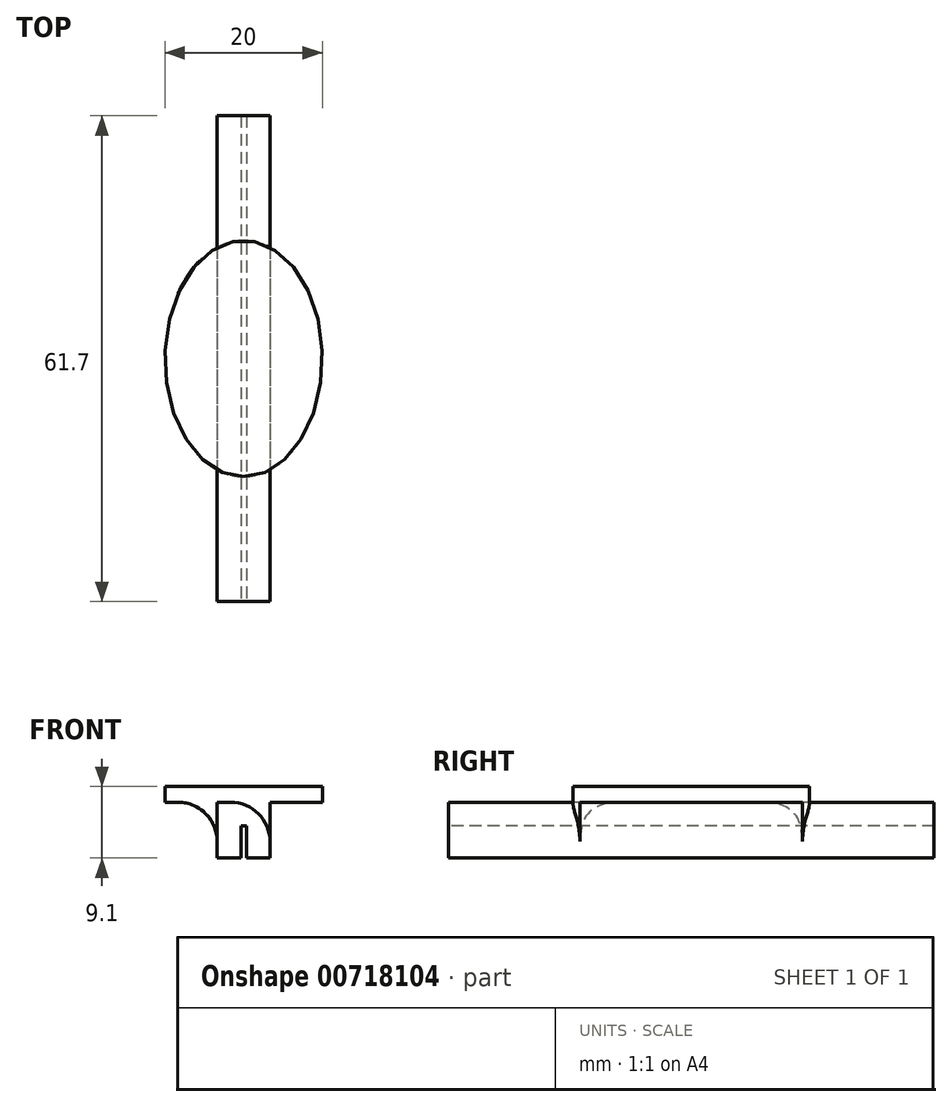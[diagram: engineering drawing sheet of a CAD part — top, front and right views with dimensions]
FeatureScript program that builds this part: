
annotation { "Feature Type Name" : "Feature", "Feature Type Description" : "" }
export const myFeature = defineFeature(function(context is Context, id is Id, definition is map)
    precondition{}
    {
        {
            var Q0;
            Q0=qCreatedBy(makeId("Front.planeOp"),FACE);
            var sketch = newSketch(context, id + "F0", { "sketchPlane" : qUnion([Q0])});
            skLineSegment(sketch, "E0", {"start": v(-3.3, 0) * mm, "end": v(3.93, 0) * mm, "construction": true});
            skLineSegment(sketch, "E1", {"start": v(0, 4.88) * mm, "end": v(0, -4.34) * mm, "construction": true});
            skLineSegment(sketch, "E2", {"start": v(-3.35, 0) * mm, "end": v(-0.35, 0) * mm});
            skLineSegment(sketch, "E3", {"start": v(-0.35, 0) * mm, "end": v(-0.35, 4.1) * mm});
            skLineSegment(sketch, "E4", {"start": v(-0.35, 4.1) * mm, "end": v(0.35, 4.1) * mm});
            skLineSegment(sketch, "E5", {"start": v(0.35, 4.1) * mm, "end": v(0.35, 0) * mm});
            skLineSegment(sketch, "E6", {"start": v(0.35, 0) * mm, "end": v(3.35, 0) * mm});
            skLineSegment(sketch, "E7", {"start": v(3.35, 0) * mm, "end": v(3.35, 7.1) * mm});
            skLineSegment(sketch, "E8", {"start": v(3.35, 7.1) * mm, "end": v(-3.35, 7.1) * mm});
            skLineSegment(sketch, "E9", {"start": v(-3.35, 7.1) * mm, "end": v(-3.35, 0) * mm});
            skSolve(sketch);
        }
        {
            var Q0;
            Q0 = qSketchRegion(id + "F0", true);
            extrude(context, id + "F1", {"entities" : qUnion([Q0]), "oppositeDirection" : true, "depth" : 61.7 * mm, "offsetDistance" : 25 * mm});
        }
        {
            var Q0;
            Q0=makeQuery(id+"F1.opExtrude","SWEPT_FACE",FACE,{"disambiguationData":[OSD([sQuery(id+"F0.wireOp",EDGE,"E8")])]});
            var sketch = newSketch(context, id + "F2", { "sketchPlane" : qUnion([Q0])});
            skEllipse(sketch, "E10", {"center": v(0, 30.85) * mm, "majorRadius": 15 * mm, "minorRadius": 10 * mm, "majorAxis": v(0, -1)});
            skLineSegment(sketch, "E11", {"start": v(0, 56.94) * mm, "end": v(0, -9.97) * mm, "construction": true});
            skPoint(sketch, "E11.endSnap0", {"position": v(0, 15.85) * mm});
            skSolve(sketch);
        }
        {
            var Q0;
            Q0 = qSketchRegion(id + "F2", true);
            extrude(context, id + "F3", {"entities" : qUnion([Q0]), "operationType" : NewBodyOperationType.ADD, "depth" : 2 * mm, "offsetDistance" : 25 * mm});
        }
        {
            var Q0;
            {var subQ0=sQuery(id+"F0.wireOp",EDGE,"E7");Q0=makeQuery(id+"F3.boolean.opBoolean","SPLIT",EDGE,{"disambiguationData":[topologyDisambiguationEdgeConnected([makeQuery(id+"F1.opExtrude","SWEPT_FACE",FACE,{"disambiguationData":[OSD([subQ0])]}),makeQuery(id+"F3.opExtrude","CAP_FACE",FACE,{"disambiguationData":[OSD([sQuery(id+"F2.wireOp",EDGE,"E10")])],"isStart":true})])],"derivedFrom":makeQuery(id+"F1.opExtrude","SWEPT_EDGE",EDGE,{"disambiguationData":[OSD([subQ0,sQuery(id+"F0.wireOp",EDGE,"E8")])]})});}
            fillet(context, id + "F4", {"entities" : qUnion([Q0]), "radius" : 5 * mm, "tangentPropagation" : true, "allowEdgeOverflow" : false});
        }
        {
            var Q0;
            {var subQ0=sQuery(id+"F0.wireOp",EDGE,"E9");Q0=makeQuery(id+"F3.boolean.opBoolean","SPLIT",EDGE,{"disambiguationData":[topologyDisambiguationEdgeConnected([makeQuery(id+"F1.opExtrude","SWEPT_FACE",FACE,{"disambiguationData":[OSD([subQ0])]}),makeQuery(id+"F3.opExtrude","CAP_FACE",FACE,{"disambiguationData":[OSD([sQuery(id+"F2.wireOp",EDGE,"E10")])],"isStart":true})])],"derivedFrom":makeQuery(id+"F1.opExtrude","SWEPT_EDGE",EDGE,{"disambiguationData":[OSD([sQuery(id+"F0.wireOp",EDGE,"E8"),subQ0])]})});}
            fillet(context, id + "F5", {"entities" : qUnion([Q0]), "radius" : 5 * mm, "tangentPropagation" : true, "allowEdgeOverflow" : false});
        }
    });
